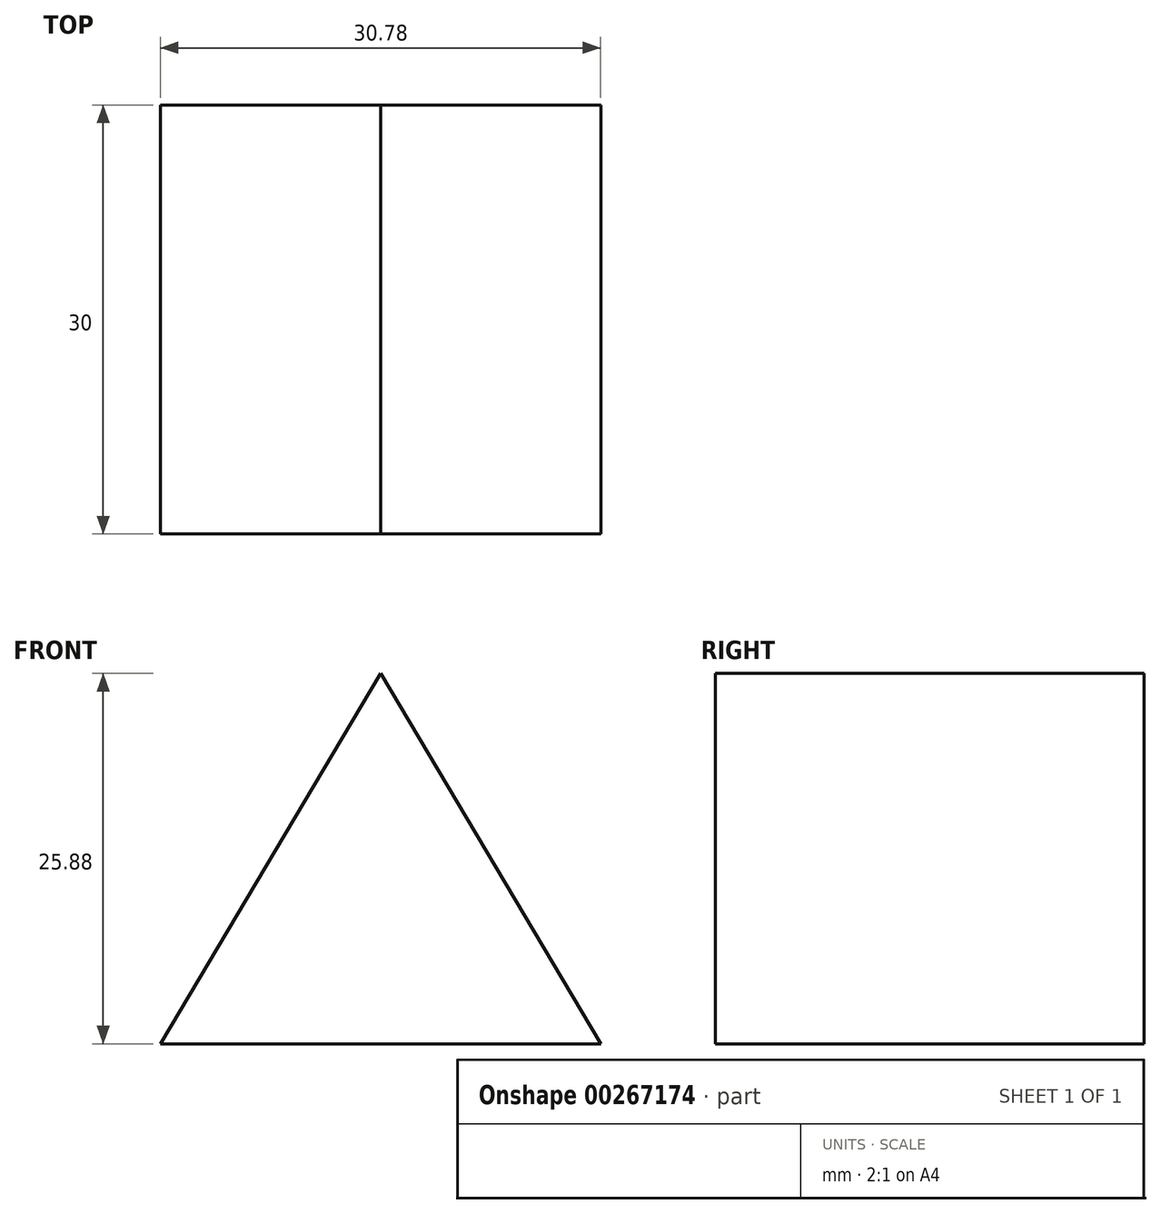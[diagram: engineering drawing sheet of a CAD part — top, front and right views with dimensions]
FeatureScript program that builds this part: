
annotation { "Feature Type Name" : "Feature", "Feature Type Description" : "" }
export const myFeature = defineFeature(function(context is Context, id is Id, definition is map)
    precondition{}
    {
        {
            var Q0;
            Q0=qCreatedBy(makeId("Front.planeOp"),FACE);
            var sketch = newSketch(context, id + "F0", { "sketchPlane" : qUnion([Q0])});
            skLineSegment(sketch, "E0", {"start": v(11.2, 0) * mm, "end": v(26.58, 25.88) * mm});
            skLineSegment(sketch, "E1", {"start": v(26.58, 25.88) * mm, "end": v(41.97, 0) * mm});
            skLineSegment(sketch, "E2", {"start": v(11.2, 0) * mm, "end": v(41.97, 0) * mm});
            skSolve(sketch);
        }
        {
            var Q0;
            Q0=makeQuery(id+"F0.imprint","IMPRINT",FACE,{"disambiguationData":[TD([[makeQuery(id+"F0.imprint","IMPRINT",EDGE,{"derivedFrom":sQuery(id+"F0.wireOp",EDGE,"E0")}),-1.0]])]});
            extrude(context, id + "F1", {"entities" : qUnion([Q0]), "depth" : 30 * mm});
        }
    });
